# Revit family: ПИК ЭНЕРГО UE Напольный лючок круглый, тройной, глухой UEBD3 R
name_source: partatom
category: Соединительные детали кабельных лотков
revit_build: Autodesk Revit 2015 (Build: 20141119_1515(x64)
units: mm (PartAtom-declared; Revit-internal decimal feet)

## types (2) — shared parameters
Отметка по умолчанию = 1219 мм
Рзм.B = 330 мм
Рзм.E = 307 мм
Рзм.H = 65 мм
Рзм.e2 = 260 мм
Рзм.e3 = 301 мм
Рзм.e4 = 280 мм
Рзм.t = 8 мм
Рзм.t2 = 4 мм
Спец.URLСсылкаСоединителяЛоткаКабельногоКанала = http://www.pik-energo.ru
Спец.ЕдИзмСоединителяЛоткаКабельногоКанала = шт.
Спец.ИзготовительСоединителяЛоткаКабельногоКанала = ПИК-ЭНЕРГО
Спец.МассаТекстСоединителяЛоткаКабельногоКанала = 1.87
Спец.НаименованиеИТенхХарСоединителяЛоткаКабельногоКанала = Монтажная крышка, круглая

## per-type parameters (varying)
| type | Пр.НаименованиеСоединителяЛоткаКабельногоКанала |
| UEBD3-R-S | Круглый лючек из полиамида с напольной рамкой, RAL 9011 |
| UEBD3-R-G | Круглый лючек из полиамида с напольной рамкой, RAL 7011 |

note: column(s) folded — value = type name in every type: Спец.КодОборудИзделияМатериалаСоединителяЛоткаКабельногоКанала

## geometry (parser evidence)
native form markers: Blend x2
no freeform markers — native parametric forms only
